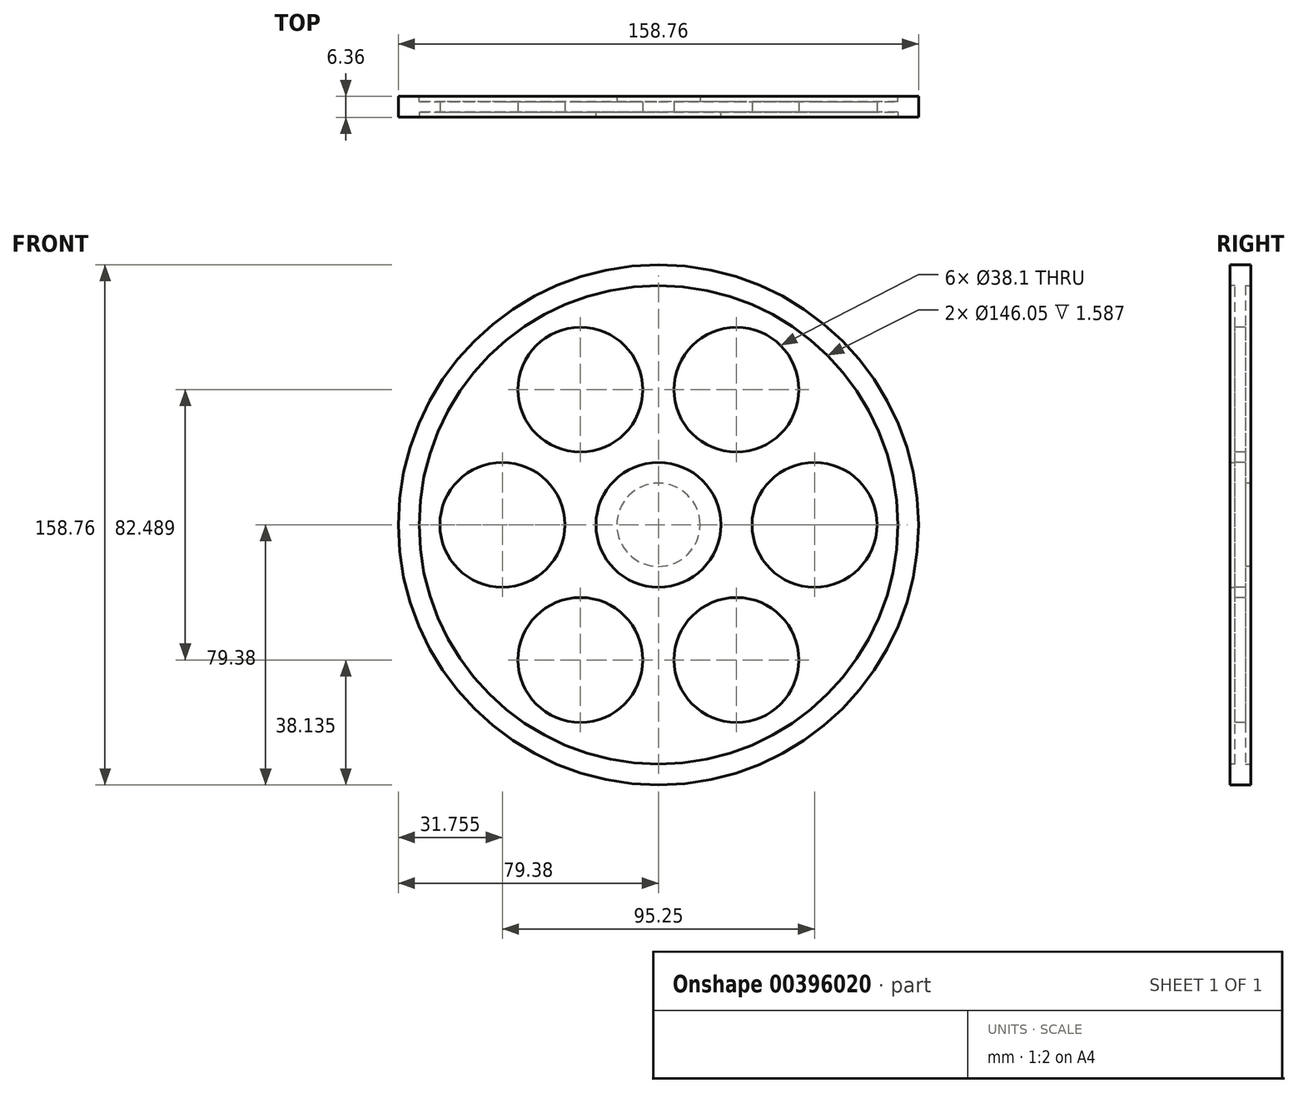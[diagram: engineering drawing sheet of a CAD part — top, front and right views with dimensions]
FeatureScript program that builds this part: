
annotation { "Feature Type Name" : "Feature", "Feature Type Description" : "" }
export const myFeature = defineFeature(function(context is Context, id is Id, definition is map)
    precondition{}
    {
        {
            var Q0;
            Q0=qCreatedBy(makeId("Front.planeOp"),FACE);
            var sketch = newSketch(context, id + "F0", { "sketchPlane" : qUnion([Q0])});
            skCircle(sketch, "E0", {"center": v(0, 0) * mm, "radius": 79.38 * mm});
            skCircle(sketch, "E1", {"center": v(0, 0) * mm, "radius": 19.05 * mm, "construction": true});
            skCircle(sketch, "E2", {"center": v(-5.56, 18.22) * mm, "radius": 3.18 * mm, "construction": true});
            skCircle(sketch, "E3", {"center": v(5.56, -18.22) * mm, "radius": 3.18 * mm, "construction": true});
            skCircle(sketch, "E4", {"center": v(0, -31.75) * mm, "radius": 3.18 * mm, "construction": true});
            skSolve(sketch);
        }
        {
            var Q0;
            Q0 = qSketchRegion(id + "F0", true);
            extrude(context, id + "F1", {"entities" : qUnion([Q0]), "endBound" : BoundingType.SYMMETRIC, "depth" : 6.35 * mm, "offsetDistance" : 25.4 * mm});
        }
        {
            var Q0;
            Q0=makeQuery(id+"F1.opExtrude","CAP_FACE",FACE,{"disambiguationData":[OSD([sQuery(id+"F0.wireOp",EDGE,"E0")])],"isStart":false});
            var sketch = newSketch(context, id + "F2", { "sketchPlane" : qUnion([Q0])});
            skCircle(sketch, "E5", {"center": v(0, 0) * mm, "radius": 73.03 * mm});
            skSolve(sketch);
        }
        {
            var Q0;
            Q0 = qSketchRegion(id + "F2", true);
            extrude(context, id + "F3", {"entities" : qUnion([Q0]), "operationType" : NewBodyOperationType.REMOVE, "oppositeDirection" : true, "depth" : 1.59 * mm, "offsetDistance" : 25.4 * mm});
        }
        {
            var Q0;
            Q0=makeQuery(id+"F1.opExtrude","CAP_FACE",FACE,{"disambiguationData":[OSD([sQuery(id+"F0.wireOp",EDGE,"E0")])],"isStart":true});
            var sketch = newSketch(context, id + "F4", { "sketchPlane" : qUnion([Q0])});
            skCircle(sketch, "E6", {"center": v(0, 0) * mm, "radius": 73.03 * mm});
            skSolve(sketch);
        }
        {
            var Q0;
            Q0 = qSketchRegion(id + "F4", true);
            extrude(context, id + "F5", {"entities" : qUnion([Q0]), "operationType" : NewBodyOperationType.REMOVE, "oppositeDirection" : true, "depth" : 1.59 * mm, "offsetDistance" : 25.4 * mm});
        }
        {
            var Q0;
            Q0=makeQuery(id+"F3.boolean.opBoolean","COPY",FACE,{"derivedFrom":makeQuery(id+"F3.opExtrude","CAP_FACE",FACE,{"disambiguationData":[OSD([sQuery(id+"F2.wireOp",EDGE,"E5")])],"isStart":false})});
            var sketch = newSketch(context, id + "F6", { "sketchPlane" : qUnion([Q0])});
            skCircle(sketch, "E7.converted", {"center": v(0, 0) * mm, "radius": 19.05 * mm});
            skSolve(sketch);
        }
        {
            var Q0;
            Q0 = qSketchRegion(id + "F6", true);
            extrude(context, id + "F7", {"entities" : qUnion([Q0]), "operationType" : NewBodyOperationType.ADD, "depth" : 1.59 * mm, "offsetDistance" : 25.4 * mm});
        }
        {
            var Q0;
            Q0=makeQuery(id+"F3.boolean.opBoolean","COPY",FACE,{"derivedFrom":makeQuery(id+"F3.opExtrude","CAP_FACE",FACE,{"disambiguationData":[OSD([sQuery(id+"F2.wireOp",EDGE,"E5")])],"isStart":false})});
            var sketch = newSketch(context, id + "F8", { "sketchPlane" : qUnion([Q0])});
            skPoint(sketch, "E8.0.midPoint", {"position": v(0, 31.75) * mm});
            skCircle(sketch, "E9", {"center": v(-23.81, -41.24) * mm, "radius": 19.05 * mm});
            skCircle(sketch, "E10", {"center": v(-47.63, 0) * mm, "radius": 19.05 * mm});
            skCircle(sketch, "E11", {"center": v(-23.81, 41.24) * mm, "radius": 19.05 * mm});
            skCircle(sketch, "E12", {"center": v(23.81, 41.24) * mm, "radius": 19.05 * mm});
            skCircle(sketch, "E13", {"center": v(47.63, 0) * mm, "radius": 19.05 * mm});
            skCircle(sketch, "E14", {"center": v(23.81, -41.24) * mm, "radius": 19.05 * mm});
            skSolve(sketch);
        }
        {
            var Q0;
            Q0 = qSketchRegion(id + "F8", true);
            extrude(context, id + "F9", {"entities" : qUnion([Q0]), "operationType" : NewBodyOperationType.REMOVE, "oppositeDirection" : true, "depth" : 25.4 * mm, "offsetDistance" : 25.4 * mm});
        }
        {
            var Q0;
            Q0=makeQuery(id+"F5.boolean.opBoolean","COPY",FACE,{"derivedFrom":makeQuery(id+"F5.opExtrude","CAP_FACE",FACE,{"disambiguationData":[OSD([sQuery(id+"F4.wireOp",EDGE,"E6")])],"isStart":false})});
            var sketch = newSketch(context, id + "F10", { "sketchPlane" : qUnion([Q0])});
            skCircle(sketch, "E15", {"center": v(0, 0) * mm, "radius": 12.7 * mm});
            skSolve(sketch);
        }
        {
            var Q0;
            Q0 = qSketchRegion(id + "F10", true);
            extrude(context, id + "F11", {"entities" : qUnion([Q0]), "operationType" : NewBodyOperationType.ADD, "depth" : 1.59 * mm, "offsetDistance" : 25.4 * mm});
        }
    });
